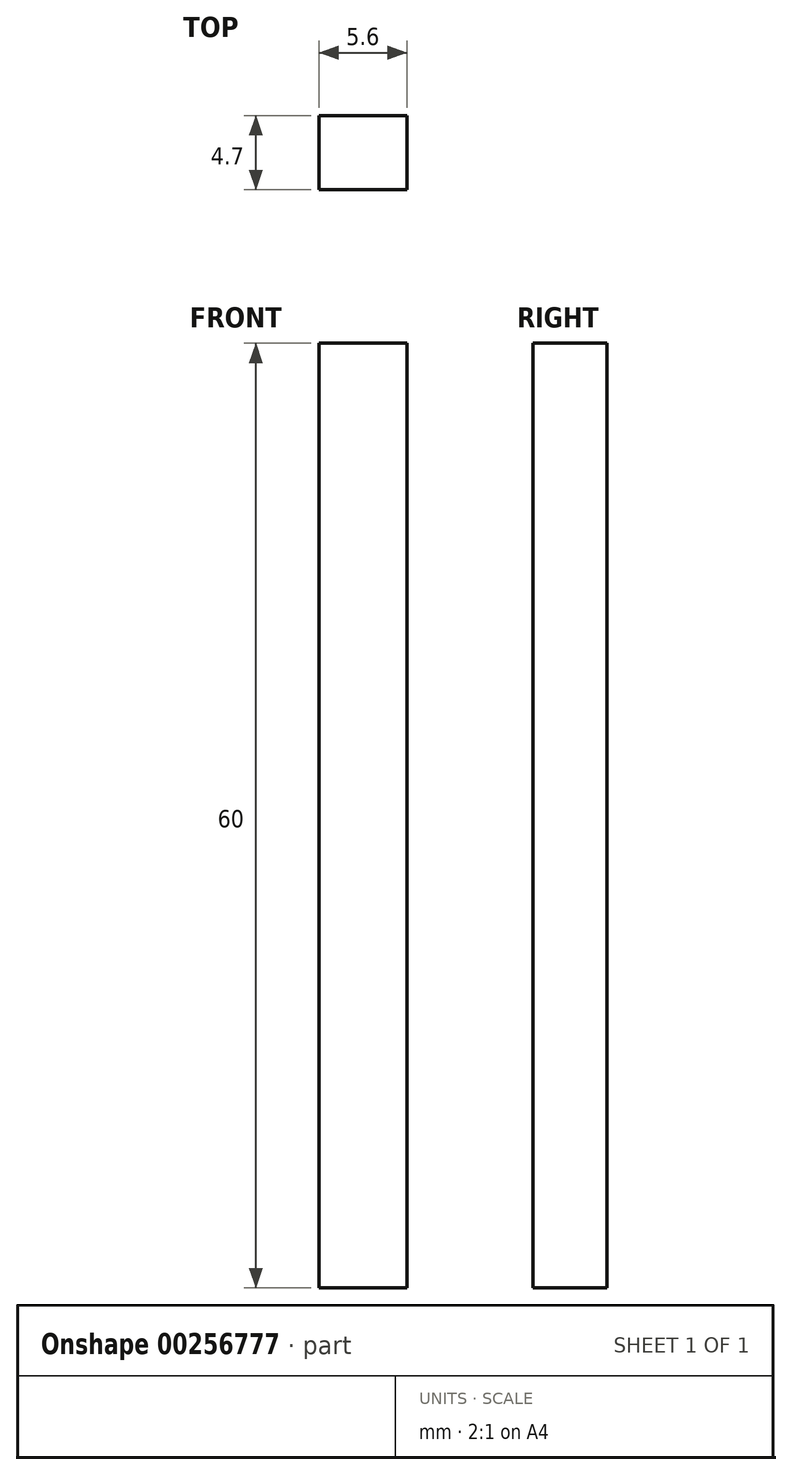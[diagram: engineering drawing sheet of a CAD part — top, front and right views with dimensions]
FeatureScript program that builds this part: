
annotation { "Feature Type Name" : "Feature", "Feature Type Description" : "" }
export const myFeature = defineFeature(function(context is Context, id is Id, definition is map)
    precondition{}
    {
        {
            var Q0;
            Q0=qCreatedBy(makeId("Top.planeOp"),FACE);
            var sketch = newSketch(context, id + "F0", { "sketchPlane" : qUnion([Q0])});
            skLineSegment(sketch, "E0.bottom", {"start": v(2.8, 2.35) * mm, "end": v(-2.8, 2.35) * mm});
            skLineSegment(sketch, "E0.top", {"start": v(2.8, -2.35) * mm, "end": v(-2.8, -2.35) * mm});
            skLineSegment(sketch, "E0.left", {"start": v(2.8, 2.35) * mm, "end": v(2.8, -2.35) * mm});
            skLineSegment(sketch, "E0.right", {"start": v(-2.8, 2.35) * mm, "end": v(-2.8, -2.35) * mm});
            skPoint(sketch, "E0.middle", {"position": v(0, 0) * mm});
            skSolve(sketch);
        }
        {
            var Q0;
            Q0=makeQuery(id+"F0.imprint","IMPRINT",FACE,{"disambiguationData":[TD([[makeQuery(id+"F0.imprint","IMPRINT",EDGE,{"derivedFrom":sQuery(id+"F0.wireOp",EDGE,"E0.bottom")}),1.0]])]});
            extrude(context, id + "F1", {"entities" : qUnion([Q0]), "depth" : 60 * mm});
        }
    });
